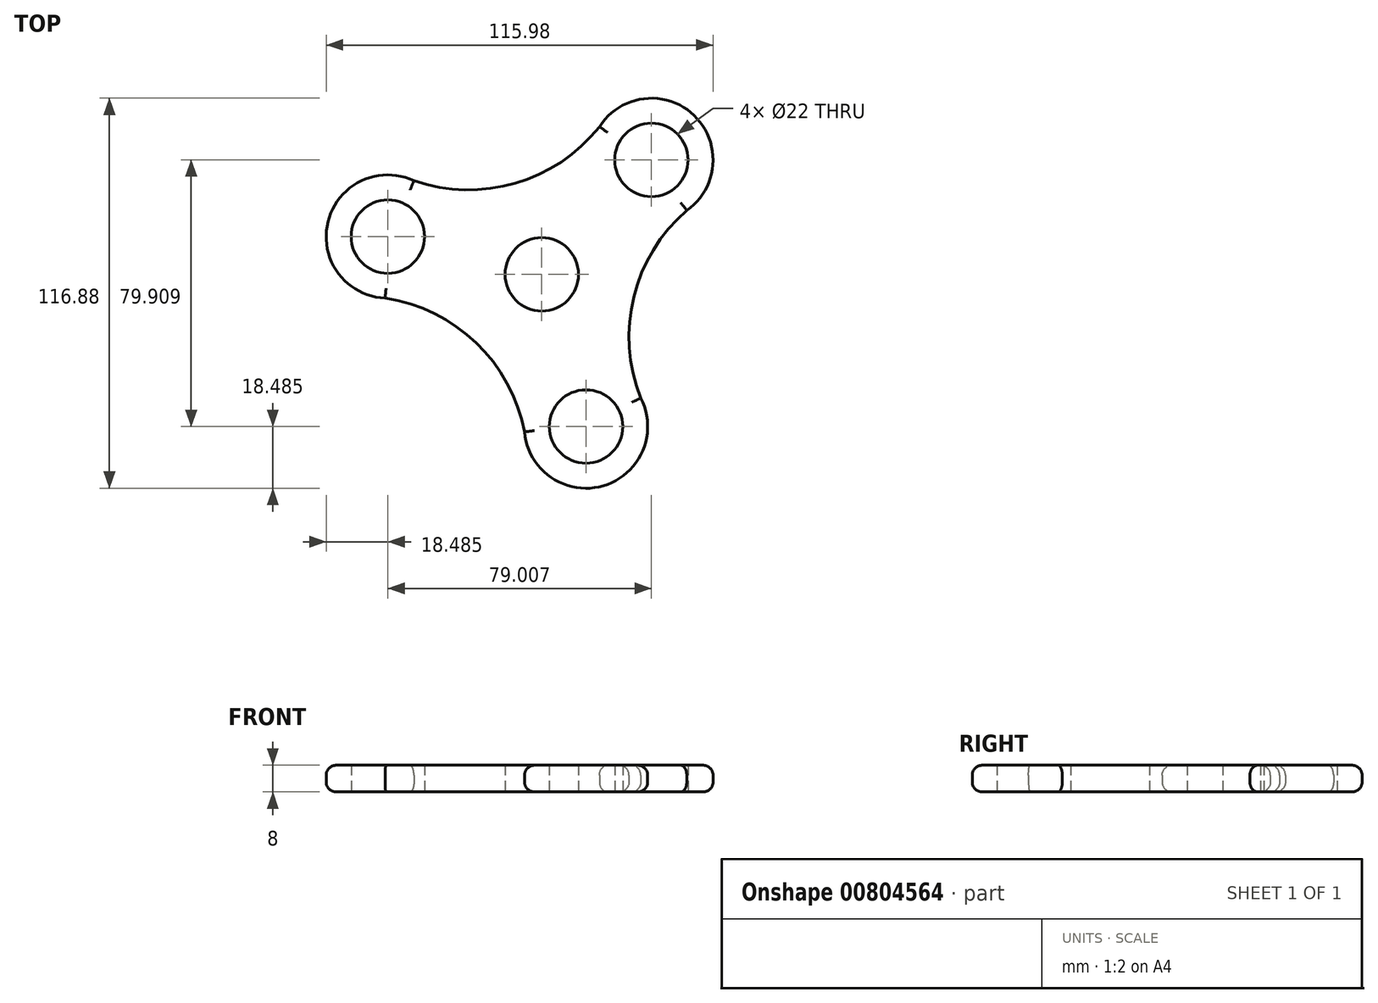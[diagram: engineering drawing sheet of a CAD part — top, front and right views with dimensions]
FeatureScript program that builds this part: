
annotation { "Feature Type Name" : "Feature", "Feature Type Description" : "" }
export const myFeature = defineFeature(function(context is Context, id is Id, definition is map)
    precondition{}
    {
        {
            var Q0;
            Q0=qCreatedBy(makeId("Top.planeOp"),FACE);
            var sketch = newSketch(context, id + "F0", { "sketchPlane" : qUnion([Q0])});
            skCircle(sketch, "E0.cCircle", {"center": v(0, 0) * mm, "radius": 33 * mm, "construction": true});
            skLineSegment(sketch, "E0.0", {"start": v(-64.09, 15.73) * mm, "end": v(45.66, 47.64) * mm, "construction": true});
            skLineSegment(sketch, "E0.1", {"start": v(45.66, 47.64) * mm, "end": v(18.43, -63.37) * mm, "construction": true});
            skLineSegment(sketch, "E0.2", {"start": v(18.43, -63.37) * mm, "end": v(-64.09, 15.73) * mm, "construction": true});
            skPoint(sketch, "E0.0.midPoint", {"position": v(-9.21, 31.68) * mm});
            skLineSegment(sketch, "E1", {"start": v(0, 0) * mm, "end": v(45.66, 47.64) * mm, "construction": true});
            skLineSegment(sketch, "E2", {"start": v(0, 0) * mm, "end": v(18.43, -63.37) * mm, "construction": true});
            skLineSegment(sketch, "E3", {"start": v(0, 0) * mm, "end": v(-64.09, 15.73) * mm, "construction": true});
            skCircle(sketch, "E4", {"center": v(0, 0) * mm, "radius": 47.5 * mm, "construction": true});
            skCircle(sketch, "E5", {"center": v(0, 0) * mm, "radius": 11 * mm});
            skCircle(sketch, "E6", {"center": v(32.87, 34.3) * mm, "radius": 11 * mm});
            skCircle(sketch, "E7", {"center": v(13.26, -45.61) * mm, "radius": 11 * mm});
            skCircle(sketch, "E8", {"center": v(-46.14, 11.32) * mm, "radius": 11 * mm});
            skCircle(sketch, "E9", {"center": v(-46.14, 11.32) * mm, "radius": 18.49 * mm});
            skCircle(sketch, "E10", {"center": v(32.87, 34.3) * mm, "radius": 18.49 * mm});
            skCircle(sketch, "E11", {"center": v(13.26, -45.61) * mm, "radius": 18.49 * mm});
            skCircle(sketch, "E12", {"center": v(0, 0) * mm, "radius": 28.22 * mm, "construction": true});
            skArc(sketch, "E13", {"start": v(-5.15, -47.22) * mm, "mid": v(-19.67, -20.52) * mm, "end": v(-46.96, -7.15) * mm});
            skArc(sketch, "E14", {"start": v(-38.32, 28.07) * mm, "mid": v(-7.94, 27.29) * mm, "end": v(17.3, 44.25) * mm});
            skArc(sketch, "E15", {"start": v(43.47, 19.15) * mm, "mid": v(27.6, -6.77) * mm, "end": v(29.67, -37.1) * mm});
            skSolve(sketch);
        }
        {
            var Q0;
            Q0 = qSketchRegion(id + "F0", true);
            extrude(context, id + "F1", {"entities" : qUnion([Q0]), "depth" : 8 * mm, "offsetDistance" : 25 * mm});
        }
        {
            var Q0;
            Q0=makeQuery(id+"F1.opExtrude","CAP_EDGE",EDGE,{"disambiguationData":[OSD([sQuery(id+"F0.wireOp",EDGE,"E14")])],"isStart":true});
            var Q1;
            Q1=makeQuery(id+"F1.opExtrude","CAP_EDGE",EDGE,{"disambiguationData":[OSD([sQuery(id+"F0.wireOp",EDGE,"E10")])],"isStart":true});
            var Q2;
            Q2=makeQuery(id+"F1.opExtrude","CAP_EDGE",EDGE,{"disambiguationData":[OSD([sQuery(id+"F0.wireOp",EDGE,"E15")])],"isStart":true});
            var Q3;
            Q3=makeQuery(id+"F1.opExtrude","CAP_EDGE",EDGE,{"disambiguationData":[OSD([sQuery(id+"F0.wireOp",EDGE,"E11")])],"isStart":true});
            var Q4;
            Q4=makeQuery(id+"F1.opExtrude","CAP_EDGE",EDGE,{"disambiguationData":[OSD([sQuery(id+"F0.wireOp",EDGE,"E13")])],"isStart":true});
            var Q5;
            Q5=makeQuery(id+"F1.opExtrude","CAP_EDGE",EDGE,{"disambiguationData":[OSD([sQuery(id+"F0.wireOp",EDGE,"E9")])],"isStart":true});
            var Q6;
            Q6=makeQuery(id+"F1.opExtrude","CAP_EDGE",EDGE,{"disambiguationData":[OSD([sQuery(id+"F0.wireOp",EDGE,"E10")])],"isStart":false});
            var Q7;
            Q7=makeQuery(id+"F1.opExtrude","CAP_EDGE",EDGE,{"disambiguationData":[OSD([sQuery(id+"F0.wireOp",EDGE,"E15")])],"isStart":false});
            var Q8;
            Q8=makeQuery(id+"F1.opExtrude","CAP_EDGE",EDGE,{"disambiguationData":[OSD([sQuery(id+"F0.wireOp",EDGE,"E11")])],"isStart":false});
            var Q9;
            Q9=makeQuery(id+"F1.opExtrude","CAP_EDGE",EDGE,{"disambiguationData":[OSD([sQuery(id+"F0.wireOp",EDGE,"E13")])],"isStart":false});
            var Q10;
            Q10=makeQuery(id+"F1.opExtrude","CAP_EDGE",EDGE,{"disambiguationData":[OSD([sQuery(id+"F0.wireOp",EDGE,"E9")])],"isStart":false});
            var Q11;
            Q11=makeQuery(id+"F1.opExtrude","CAP_EDGE",EDGE,{"disambiguationData":[OSD([sQuery(id+"F0.wireOp",EDGE,"E14")])],"isStart":false});
            fillet(context, id + "F2", {"entities" : qUnion([Q0, Q1, Q2, Q3, Q4, Q5, Q6, Q7, Q8, Q9, Q10, Q11]), "radius" : 3 * mm, "tangentPropagation" : true, "allowEdgeOverflow" : false});
        }
    });
